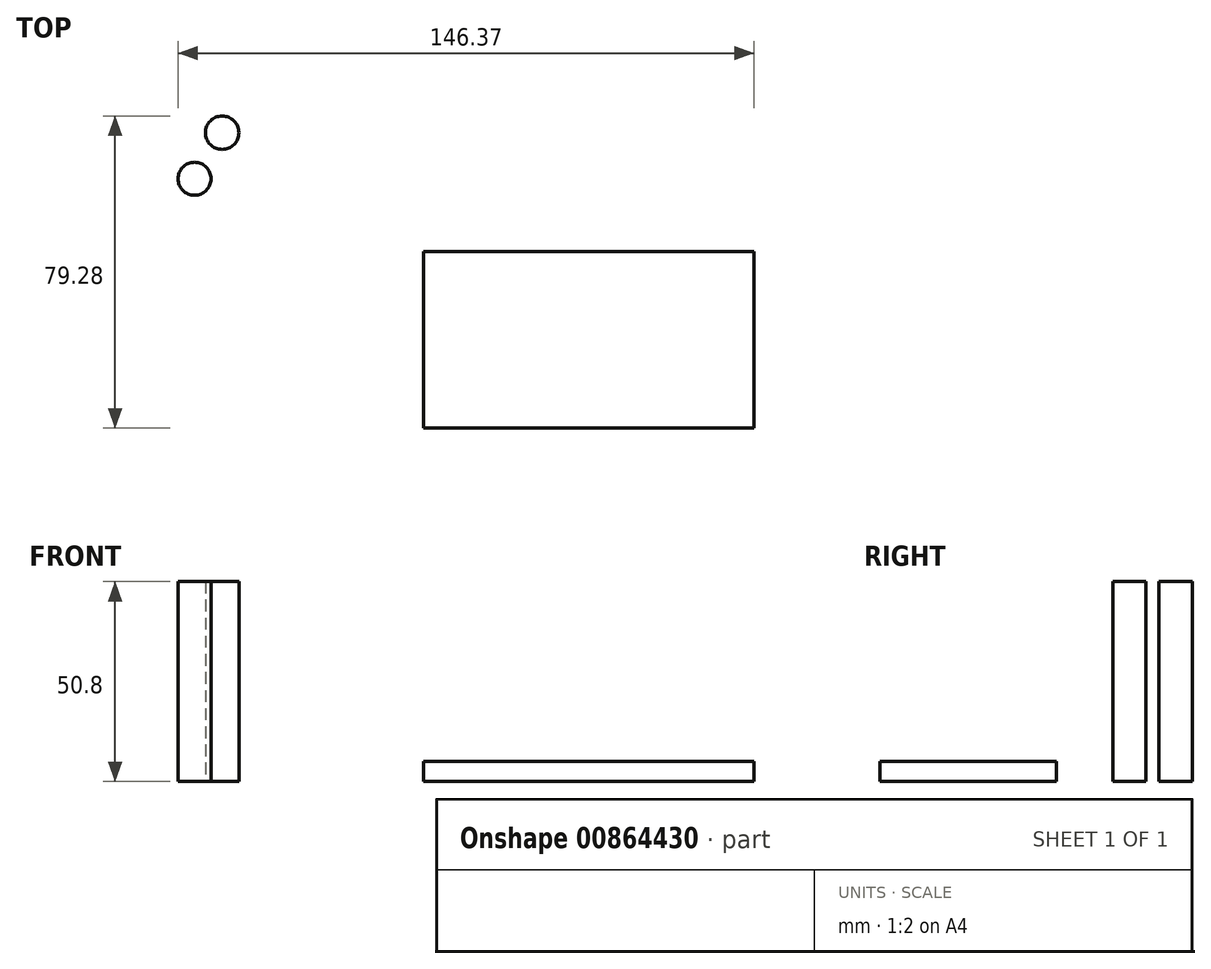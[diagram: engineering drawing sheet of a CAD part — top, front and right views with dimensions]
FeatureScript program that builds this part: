
annotation { "Feature Type Name" : "Feature", "Feature Type Description" : "" }
export const myFeature = defineFeature(function(context is Context, id is Id, definition is map)
    precondition{}
    {
        {
            var Q0;
            Q0=qCreatedBy(makeId("Top.planeOp"),FACE);
            var sketch = newSketch(context, id + "F0", { "sketchPlane" : qUnion([Q0])});
            skCircle(sketch, "E0", {"center": v(-120.3, -33.87) * mm, "radius": 4.2 * mm});
            skSolve(sketch);
        }
        {
            var Q0;
            Q0=makeQuery(id+"F0.imprint","IMPRINT",FACE,{"disambiguationData":[TD([[makeQuery(id+"F0.imprint","IMPRINT",EDGE,{"derivedFrom":sQuery(id+"F0.wireOp",EDGE,"E0")}),1.0]])]});
            extrude(context, id + "F1", {"entities" : qUnion([Q0]), "depth" : 50.8 * mm, "offsetDistance" : 25.4 * mm});
        }
        {
            var Q0;
            Q0=qCreatedBy(makeId("Top.planeOp"),FACE);
            var sketch = newSketch(context, id + "F2", { "sketchPlane" : qUnion([Q0])});
            skLineSegment(sketch, "E1.bottom", {"start": v(-62.18, -52.36) * mm, "end": v(21.87, -52.36) * mm});
            skLineSegment(sketch, "E1.top", {"start": v(-62.18, -97.2) * mm, "end": v(21.87, -97.2) * mm});
            skLineSegment(sketch, "E1.left", {"start": v(-62.18, -52.36) * mm, "end": v(-62.18, -97.2) * mm});
            skLineSegment(sketch, "E1.right", {"start": v(21.87, -52.36) * mm, "end": v(21.87, -97.2) * mm});
            skSolve(sketch);
        }
        {
            var Q0;
            Q0=makeQuery(id+"F2.imprint","IMPRINT",FACE,{"disambiguationData":[TD([[makeQuery(id+"F2.imprint","IMPRINT",EDGE,{"derivedFrom":sQuery(id+"F2.wireOp",EDGE,"E1.bottom")}),-1.0]])]});
            extrude(context, id + "F3", {"entities" : qUnion([Q0]), "depth" : 5.08 * mm, "offsetDistance" : 25.4 * mm});
        }
        {
            var Q0;
            Q0=qCreatedBy(makeId("Top.planeOp"),FACE);
            var sketch = newSketch(context, id + "F4", { "sketchPlane" : qUnion([Q0])});
            skCircle(sketch, "E2", {"center": v(-113.29, -22.17) * mm, "radius": 4.24 * mm});
            skSolve(sketch);
        }
        {
            var Q0;
            Q0=makeQuery(id+"F4.imprint","IMPRINT",FACE,{"disambiguationData":[TD([[makeQuery(id+"F4.imprint","IMPRINT",EDGE,{"derivedFrom":sQuery(id+"F4.wireOp",EDGE,"E2")}),1.0]])]});
            extrude(context, id + "F5", {"entities" : qUnion([Q0]), "depth" : 50.8 * mm, "offsetDistance" : 25.4 * mm});
        }
    });
